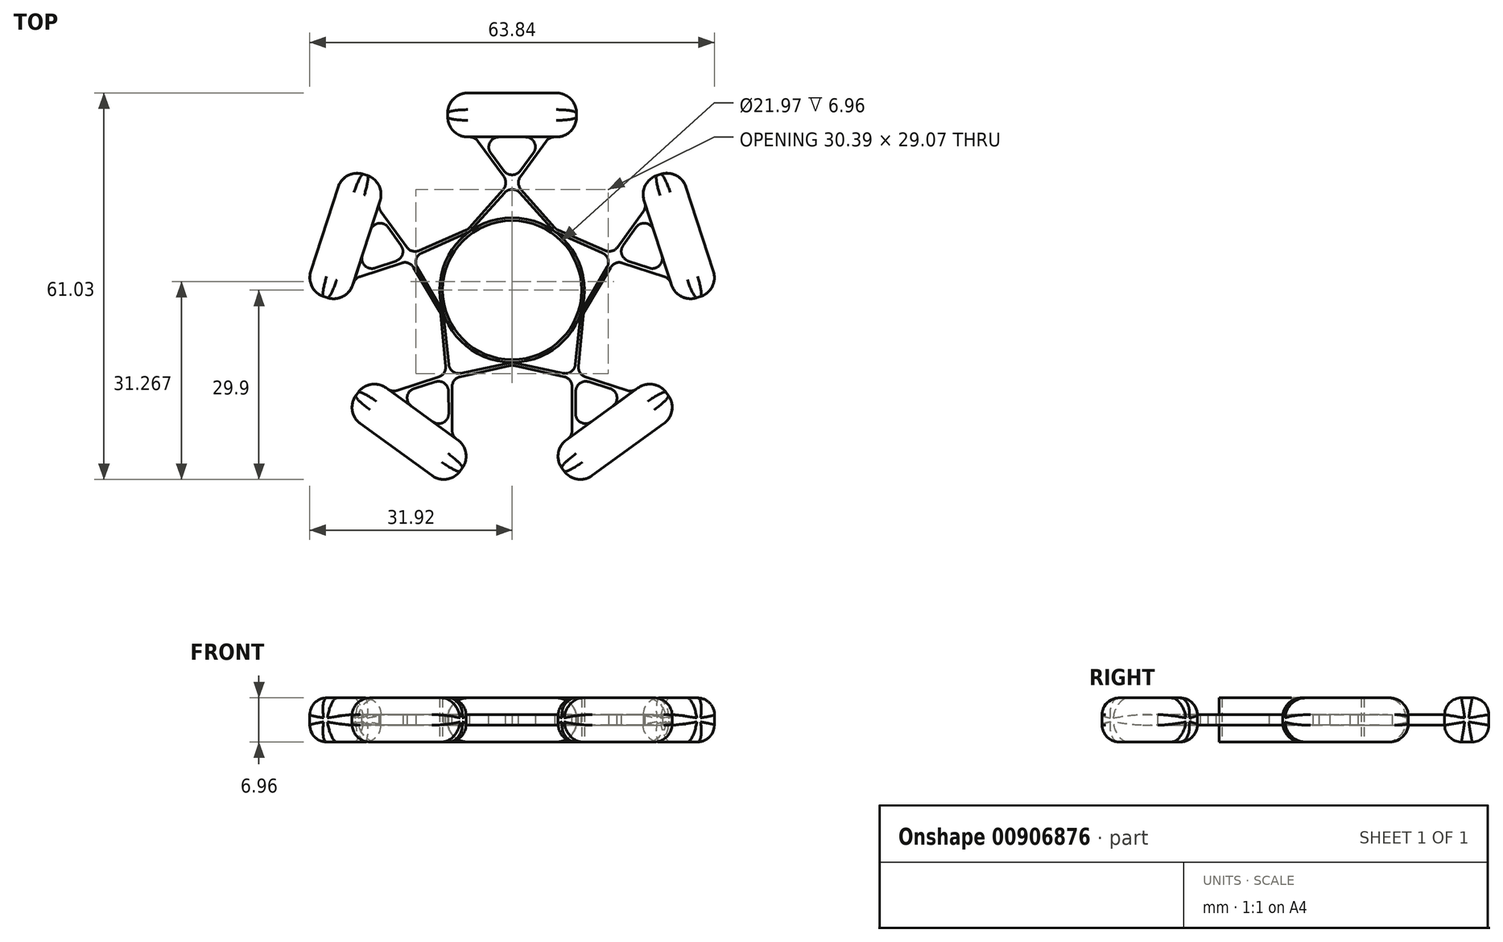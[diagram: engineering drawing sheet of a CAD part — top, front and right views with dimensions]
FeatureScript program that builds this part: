
annotation { "Feature Type Name" : "Feature", "Feature Type Description" : "" }
export const myFeature = defineFeature(function(context is Context, id is Id, definition is map)
    precondition{}
    {
        {
            var Q0;
            Q0=qCreatedBy(makeId("Top.planeOp"),FACE);
            var sketch = newSketch(context, id + "F0", { "sketchPlane" : qUnion([Q0])});
            skCircle(sketch, "E0", {"center": v(0, 0) * mm, "radius": 11.43 * mm});
            skCircle(sketch, "E1", {"center": v(0, 0) * mm, "radius": 10.99 * mm});
            skSolve(sketch);
        }
        {
            var Q0;
            Q0=makeQuery(id+"F0.imprint","IMPRINT",FACE,{"disambiguationData":[TD([[makeQuery(id+"F0.imprint","IMPRINT",EDGE,{"derivedFrom":sQuery(id+"F0.wireOp",EDGE,"E0")}),1.0]])]});
            extrude(context, id + "F1", {"entities" : qUnion([Q0]), "depth" : 6.96 * mm, "offsetDistance" : 25.4 * mm, "symmetric" : true});
        }
        {
            var Q0;
            Q0=qCreatedBy(makeId("Top.planeOp"),FACE);
            var sketch = newSketch(context, id + "F2", { "sketchPlane" : qUnion([Q0])});
            skLineSegment(sketch, "E2", {"start": v(-6.97, 9.58) * mm, "end": v(-0.55, 16.86) * mm});
            skLineSegment(sketch, "E3", {"start": v(-0.55, 16.86) * mm, "end": v(-5.87, 24.17) * mm});
            skLineSegment(sketch, "E4", {"start": v(-6.71, 9.24) * mm, "end": v(0, 16.69) * mm});
            skLineSegment(sketch, "E5", {"start": v(-5.25, 24.17) * mm, "end": v(0, 17.12) * mm});
            skLineSegment(sketch, "E6.MirrorCS", {"start": v(5.25, 24.17) * mm, "end": v(0, 17.12) * mm});
            skLineSegment(sketch, "E7.MirrorCS", {"start": v(6.71, 9.24) * mm, "end": v(0, 16.69) * mm});
            skLineSegment(sketch, "E8.MirrorCS", {"start": v(0.55, 16.86) * mm, "end": v(5.87, 24.17) * mm});
            skLineSegment(sketch, "E9.MirrorCS", {"start": v(6.97, 9.58) * mm, "end": v(0.55, 16.86) * mm});
            skLineSegment(sketch, "E10.1.0", {"start": v(-21.37, 12.47) * mm, "end": v(-16.28, 5.3) * mm});
            skLineSegment(sketch, "E10.1.1", {"start": v(-16.2, 4.68) * mm, "end": v(-24.8, 1.88) * mm});
            skLineSegment(sketch, "E10.1.2", {"start": v(-11.27, -3.67) * mm, "end": v(-16.2, 4.68) * mm});
            skLineSegment(sketch, "E10.1.3", {"start": v(-6.71, 9.24) * mm, "end": v(-15.87, 5.16) * mm});
            skLineSegment(sketch, "E10.1.4", {"start": v(-15.86, 5.74) * mm, "end": v(-21.18, 13.06) * mm});
            skLineSegment(sketch, "E10.1.5", {"start": v(-6.96, 9.6) * mm, "end": v(-15.86, 5.74) * mm});
            skLineSegment(sketch, "E10.1.6", {"start": v(-10.86, -3.53) * mm, "end": v(-15.87, 5.16) * mm});
            skLineSegment(sketch, "E10.1.7", {"start": v(-24.61, 2.47) * mm, "end": v(-16.28, 5.3) * mm});
            skLineSegment(sketch, "E10.2.0", {"start": v(-18.46, -16.47) * mm, "end": v(-10.06, -13.85) * mm});
            skLineSegment(sketch, "E10.2.1", {"start": v(-9.46, -13.97) * mm, "end": v(-9.46, -23) * mm});
            skLineSegment(sketch, "E10.2.2", {"start": v(0, -11.85) * mm, "end": v(-9.46, -13.97) * mm});
            skLineSegment(sketch, "E10.2.3", {"start": v(-10.86, -3.53) * mm, "end": v(-9.8, -13.5) * mm});
            skLineSegment(sketch, "E10.2.4", {"start": v(-10.36, -13.32) * mm, "end": v(-18.96, -16.1) * mm});
            skLineSegment(sketch, "E10.2.5", {"start": v(-11.27, -3.65) * mm, "end": v(-10.36, -13.32) * mm});
            skLineSegment(sketch, "E10.2.6", {"start": v(0, -11.42) * mm, "end": v(-9.8, -13.5) * mm});
            skLineSegment(sketch, "E10.2.7", {"start": v(-9.96, -22.65) * mm, "end": v(-10.06, -13.85) * mm});
            skLineSegment(sketch, "E10.3.0", {"start": v(9.96, -22.65) * mm, "end": v(10.06, -13.85) * mm});
            skLineSegment(sketch, "E10.3.1", {"start": v(10.36, -13.32) * mm, "end": v(18.96, -16.1) * mm});
            skLineSegment(sketch, "E10.3.2", {"start": v(11.27, -3.65) * mm, "end": v(10.36, -13.32) * mm});
            skLineSegment(sketch, "E10.3.3", {"start": v(0, -11.42) * mm, "end": v(9.8, -13.5) * mm});
            skLineSegment(sketch, "E10.3.4", {"start": v(9.46, -13.97) * mm, "end": v(9.46, -23) * mm});
            skLineSegment(sketch, "E10.3.5", {"start": v(0, -11.85) * mm, "end": v(9.46, -13.97) * mm});
            skLineSegment(sketch, "E10.3.6", {"start": v(10.86, -3.53) * mm, "end": v(9.8, -13.5) * mm});
            skLineSegment(sketch, "E10.3.7", {"start": v(18.46, -16.47) * mm, "end": v(10.06, -13.85) * mm});
            skLineSegment(sketch, "E10.4.0", {"start": v(24.61, 2.47) * mm, "end": v(16.28, 5.3) * mm});
            skLineSegment(sketch, "E10.4.1", {"start": v(15.86, 5.74) * mm, "end": v(21.18, 13.06) * mm});
            skLineSegment(sketch, "E10.4.2", {"start": v(6.96, 9.6) * mm, "end": v(15.86, 5.74) * mm});
            skLineSegment(sketch, "E10.4.3", {"start": v(10.86, -3.53) * mm, "end": v(15.87, 5.16) * mm});
            skLineSegment(sketch, "E10.4.4", {"start": v(16.2, 4.68) * mm, "end": v(24.8, 1.88) * mm});
            skLineSegment(sketch, "E10.4.5", {"start": v(11.27, -3.67) * mm, "end": v(16.2, 4.68) * mm});
            skLineSegment(sketch, "E10.4.6", {"start": v(6.71, 9.24) * mm, "end": v(15.87, 5.16) * mm});
            skLineSegment(sketch, "E10.4.7", {"start": v(21.37, 12.47) * mm, "end": v(16.28, 5.3) * mm});
            skPoint(sketch, "E10.center", {"position": v(0, 0) * mm});
            skLineSegment(sketch, "E11", {"start": v(-5.87, 24.17) * mm, "end": v(-5.25, 24.17) * mm});
            skLineSegment(sketch, "E12.MirrorCS", {"start": v(5.87, 24.17) * mm, "end": v(5.25, 24.17) * mm});
            skLineSegment(sketch, "E13.1.0", {"start": v(-21.18, 13.06) * mm, "end": v(-21.37, 12.47) * mm});
            skLineSegment(sketch, "E13.1.1", {"start": v(-24.8, 1.88) * mm, "end": v(-24.61, 2.47) * mm});
            skLineSegment(sketch, "E13.2.0", {"start": v(-18.96, -16.1) * mm, "end": v(-18.46, -16.47) * mm});
            skLineSegment(sketch, "E13.2.1", {"start": v(-9.46, -23) * mm, "end": v(-9.96, -22.65) * mm});
            skLineSegment(sketch, "E13.3.0", {"start": v(9.46, -23) * mm, "end": v(9.96, -22.65) * mm});
            skLineSegment(sketch, "E13.3.1", {"start": v(18.96, -16.1) * mm, "end": v(18.46, -16.47) * mm});
            skLineSegment(sketch, "E13.4.0", {"start": v(24.8, 1.88) * mm, "end": v(24.61, 2.47) * mm});
            skLineSegment(sketch, "E13.4.1", {"start": v(21.18, 13.06) * mm, "end": v(21.37, 12.47) * mm});
            skSolve(sketch);
        }
        {
            var Q0;
            Q0 = qSketchRegion(id + "F2", true);
            extrude(context, id + "F3", {"entities" : qUnion([Q0]), "depth" : 1.65 * mm, "offsetDistance" : 25.4 * mm, "symmetric" : true});
        }
        {
            var Q0;
            Q0=qCreatedBy(makeId("Top.planeOp"),FACE);
            var sketch = newSketch(context, id + "F4", { "sketchPlane" : qUnion([Q0])});
            skLineSegment(sketch, "E14.bottom", {"start": v(10.16, 24.17) * mm, "end": v(-10.16, 24.17) * mm});
            skLineSegment(sketch, "E14.top", {"start": v(10.16, 31.13) * mm, "end": v(-10.16, 31.13) * mm});
            skLineSegment(sketch, "E14.left", {"start": v(10.16, 24.17) * mm, "end": v(10.16, 31.13) * mm});
            skLineSegment(sketch, "E14.right", {"start": v(-10.16, 24.17) * mm, "end": v(-10.16, 31.13) * mm});
            skPoint(sketch, "E14.middle", {"position": v(0, 27.65) * mm});
            skLineSegment(sketch, "E15.1.0", {"start": v(-19.85, 17.13) * mm, "end": v(-26.13, -2.2) * mm});
            skPoint(sketch, "E15.1.1", {"position": v(-26.3, 8.55) * mm});
            skLineSegment(sketch, "E15.1.2", {"start": v(-19.85, 17.13) * mm, "end": v(-26.47, 19.28) * mm});
            skLineSegment(sketch, "E15.1.3", {"start": v(-26.47, 19.28) * mm, "end": v(-32.75, -0.04) * mm});
            skLineSegment(sketch, "E15.1.4", {"start": v(-26.13, -2.2) * mm, "end": v(-32.75, -0.04) * mm});
            skLineSegment(sketch, "E15.2.0", {"start": v(-22.43, -13.58) * mm, "end": v(-5.99, -25.53) * mm});
            skPoint(sketch, "E15.2.1", {"position": v(-16.25, -22.37) * mm});
            skLineSegment(sketch, "E15.2.2", {"start": v(-22.43, -13.58) * mm, "end": v(-26.52, -19.22) * mm});
            skLineSegment(sketch, "E15.2.3", {"start": v(-26.52, -19.22) * mm, "end": v(-10.08, -31.16) * mm});
            skLineSegment(sketch, "E15.2.4", {"start": v(-5.99, -25.53) * mm, "end": v(-10.08, -31.16) * mm});
            skLineSegment(sketch, "E15.3.0", {"start": v(5.99, -25.53) * mm, "end": v(22.43, -13.58) * mm});
            skPoint(sketch, "E15.3.1", {"position": v(16.25, -22.37) * mm});
            skLineSegment(sketch, "E15.3.2", {"start": v(5.99, -25.53) * mm, "end": v(10.08, -31.16) * mm});
            skLineSegment(sketch, "E15.3.3", {"start": v(10.08, -31.16) * mm, "end": v(26.52, -19.22) * mm});
            skLineSegment(sketch, "E15.3.4", {"start": v(22.43, -13.58) * mm, "end": v(26.52, -19.22) * mm});
            skLineSegment(sketch, "E15.4.0", {"start": v(26.13, -2.2) * mm, "end": v(19.85, 17.13) * mm});
            skPoint(sketch, "E15.4.1", {"position": v(26.3, 8.55) * mm});
            skLineSegment(sketch, "E15.4.2", {"start": v(26.13, -2.2) * mm, "end": v(32.75, -0.04) * mm});
            skLineSegment(sketch, "E15.4.3", {"start": v(32.75, -0.04) * mm, "end": v(26.47, 19.28) * mm});
            skLineSegment(sketch, "E15.4.4", {"start": v(19.85, 17.13) * mm, "end": v(26.47, 19.28) * mm});
            skPoint(sketch, "E15.center", {"position": v(0, 0) * mm});
            skSolve(sketch);
        }
        {
            var Q0;
            Q0 = qSketchRegion(id + "F4", true);
            extrude(context, id + "F5", {"entities" : qUnion([Q0]), "operationType" : NewBodyOperationType.ADD, "depth" : 6.96 * mm, "offsetDistance" : 25.4 * mm, "symmetric" : true});
        }
        {
            var Q0;
            Q0=makeQuery(id+"F3.opExtrude","SWEPT_EDGE",EDGE,{"disambiguationData":[OSD([sQuery(id+"F2.wireOp",EDGE,"E10.1.1"),sQuery(id+"F2.wireOp",EDGE,"E10.1.2")])]});
            var Q1;
            Q1=makeQuery(id+"F3.opExtrude","SWEPT_EDGE",EDGE,{"disambiguationData":[OSD([sQuery(id+"F2.wireOp",EDGE,"E10.1.4"),sQuery(id+"F2.wireOp",EDGE,"E10.1.5")])]});
            var Q2;
            Q2=makeQuery(id+"F3.opExtrude","SWEPT_EDGE",EDGE,{"disambiguationData":[OSD([sQuery(id+"F2.wireOp",EDGE,"E10.1.3"),sQuery(id+"F2.wireOp",EDGE,"E10.1.6")])]});
            var Q3;
            Q3=makeQuery(id+"F3.opExtrude","SWEPT_EDGE",EDGE,{"disambiguationData":[OSD([sQuery(id+"F2.wireOp",EDGE,"E10.1.0"),sQuery(id+"F2.wireOp",EDGE,"E10.1.7")])]});
            var Q4;
            Q4=makeQuery(id+"F5.boolean.opBoolean","INTERSECT",EDGE,{"derivedFrom":[makeQuery(id+"F3.opExtrude","SWEPT_FACE",FACE,{"disambiguationData":[OSD([sQuery(id+"F2.wireOp",EDGE,"E10.1.0")])]}),makeQuery(id+"F5.opExtrude","SWEPT_FACE",FACE,{"disambiguationData":[OSD([sQuery(id+"F4.wireOp",EDGE,"E15.1.0")])]})]});
            var Q5;
            Q5=makeQuery(id+"F5.boolean.opBoolean","INTERSECT",EDGE,{"derivedFrom":[makeQuery(id+"F3.opExtrude","SWEPT_FACE",FACE,{"disambiguationData":[OSD([sQuery(id+"F2.wireOp",EDGE,"E10.1.1")])]}),makeQuery(id+"F5.opExtrude","SWEPT_FACE",FACE,{"disambiguationData":[OSD([sQuery(id+"F4.wireOp",EDGE,"E15.1.0")])]})]});
            var Q6;
            Q6=makeQuery(id+"F5.boolean.opBoolean","INTERSECT",EDGE,{"derivedFrom":[makeQuery(id+"F3.opExtrude","SWEPT_FACE",FACE,{"disambiguationData":[OSD([sQuery(id+"F2.wireOp",EDGE,"E10.1.7")])]}),makeQuery(id+"F5.opExtrude","SWEPT_FACE",FACE,{"disambiguationData":[OSD([sQuery(id+"F4.wireOp",EDGE,"E15.1.0")])]})]});
            var Q7;
            Q7=makeQuery(id+"F5.boolean.opBoolean","INTERSECT",EDGE,{"derivedFrom":[makeQuery(id+"F3.opExtrude","SWEPT_FACE",FACE,{"disambiguationData":[OSD([sQuery(id+"F2.wireOp",EDGE,"E10.1.4")])]}),makeQuery(id+"F5.opExtrude","SWEPT_FACE",FACE,{"disambiguationData":[OSD([sQuery(id+"F4.wireOp",EDGE,"E15.1.0")])]})]});
            var Q8;
            Q8=makeQuery(id+"F3.opExtrude","SWEPT_EDGE",EDGE,{"disambiguationData":[OSD([sQuery(id+"F2.wireOp",EDGE,"E2"),sQuery(id+"F2.wireOp",EDGE,"E10.1.5")])]});
            var Q9;
            Q9=makeQuery(id+"F3.opExtrude","SWEPT_EDGE",EDGE,{"disambiguationData":[OSD([sQuery(id+"F2.wireOp",EDGE,"E10.1.2"),sQuery(id+"F2.wireOp",EDGE,"E10.2.5")])]});
            var Q10;
            Q10=makeQuery(id+"F3.opExtrude","SWEPT_EDGE",EDGE,{"disambiguationData":[OSD([sQuery(id+"F2.wireOp",EDGE,"E8.MirrorCS"),sQuery(id+"F2.wireOp",EDGE,"E9.MirrorCS")])]});
            var Q11;
            Q11=makeQuery(id+"F3.opExtrude","SWEPT_EDGE",EDGE,{"disambiguationData":[OSD([sQuery(id+"F2.wireOp",EDGE,"E9.MirrorCS"),sQuery(id+"F2.wireOp",EDGE,"E10.4.2")])]});
            var Q12;
            Q12=makeQuery(id+"F3.opExtrude","SWEPT_EDGE",EDGE,{"disambiguationData":[OSD([sQuery(id+"F2.wireOp",EDGE,"E2"),sQuery(id+"F2.wireOp",EDGE,"E3")])]});
            var Q13;
            Q13=makeQuery(id+"F3.opExtrude","SWEPT_EDGE",EDGE,{"disambiguationData":[OSD([sQuery(id+"F2.wireOp",EDGE,"E4"),sQuery(id+"F2.wireOp",EDGE,"E7.MirrorCS")])]});
            var Q14;
            Q14=makeQuery(id+"F3.opExtrude","SWEPT_EDGE",EDGE,{"disambiguationData":[OSD([sQuery(id+"F2.wireOp",EDGE,"E5"),sQuery(id+"F2.wireOp",EDGE,"E6.MirrorCS")])]});
            var Q15;
            Q15=makeQuery(id+"F5.boolean.opBoolean","INTERSECT",EDGE,{"derivedFrom":[makeQuery(id+"F3.opExtrude","SWEPT_FACE",FACE,{"disambiguationData":[OSD([sQuery(id+"F2.wireOp",EDGE,"E8.MirrorCS")])]}),makeQuery(id+"F5.opExtrude","SWEPT_FACE",FACE,{"disambiguationData":[OSD([sQuery(id+"F4.wireOp",EDGE,"E14.bottom")])]})]});
            var Q16;
            Q16=makeQuery(id+"F5.boolean.opBoolean","INTERSECT",EDGE,{"derivedFrom":[makeQuery(id+"F3.opExtrude","SWEPT_FACE",FACE,{"disambiguationData":[OSD([sQuery(id+"F2.wireOp",EDGE,"E3")])]}),makeQuery(id+"F5.opExtrude","SWEPT_FACE",FACE,{"disambiguationData":[OSD([sQuery(id+"F4.wireOp",EDGE,"E14.bottom")])]})]});
            var Q17;
            Q17=makeQuery(id+"F5.boolean.opBoolean","INTERSECT",EDGE,{"derivedFrom":[makeQuery(id+"F3.opExtrude","SWEPT_FACE",FACE,{"disambiguationData":[OSD([sQuery(id+"F2.wireOp",EDGE,"E5")])]}),makeQuery(id+"F5.opExtrude","SWEPT_FACE",FACE,{"disambiguationData":[OSD([sQuery(id+"F4.wireOp",EDGE,"E14.bottom")])]})]});
            var Q18;
            Q18=makeQuery(id+"F5.boolean.opBoolean","INTERSECT",EDGE,{"derivedFrom":[makeQuery(id+"F3.opExtrude","SWEPT_FACE",FACE,{"disambiguationData":[OSD([sQuery(id+"F2.wireOp",EDGE,"E6.MirrorCS")])]}),makeQuery(id+"F5.opExtrude","SWEPT_FACE",FACE,{"disambiguationData":[OSD([sQuery(id+"F4.wireOp",EDGE,"E14.bottom")])]})]});
            var Q19;
            Q19=makeQuery(id+"F3.opExtrude","SWEPT_EDGE",EDGE,{"disambiguationData":[OSD([sQuery(id+"F2.wireOp",EDGE,"E10.4.4"),sQuery(id+"F2.wireOp",EDGE,"E10.4.5")])]});
            var Q20;
            Q20=makeQuery(id+"F3.opExtrude","SWEPT_EDGE",EDGE,{"disambiguationData":[OSD([sQuery(id+"F2.wireOp",EDGE,"E10.3.2"),sQuery(id+"F2.wireOp",EDGE,"E10.4.5")])]});
            var Q21;
            Q21=makeQuery(id+"F5.boolean.opBoolean","INTERSECT",EDGE,{"derivedFrom":[makeQuery(id+"F3.opExtrude","SWEPT_FACE",FACE,{"disambiguationData":[OSD([sQuery(id+"F2.wireOp",EDGE,"E10.4.1")])]}),makeQuery(id+"F5.opExtrude","SWEPT_FACE",FACE,{"disambiguationData":[OSD([sQuery(id+"F4.wireOp",EDGE,"E15.4.0")])]})]});
            var Q22;
            Q22=makeQuery(id+"F3.opExtrude","SWEPT_EDGE",EDGE,{"disambiguationData":[OSD([sQuery(id+"F2.wireOp",EDGE,"E10.4.3"),sQuery(id+"F2.wireOp",EDGE,"E10.4.6")])]});
            var Q23;
            Q23=makeQuery(id+"F5.boolean.opBoolean","INTERSECT",EDGE,{"derivedFrom":[makeQuery(id+"F3.opExtrude","SWEPT_FACE",FACE,{"disambiguationData":[OSD([sQuery(id+"F2.wireOp",EDGE,"E10.4.4")])]}),makeQuery(id+"F5.opExtrude","SWEPT_FACE",FACE,{"disambiguationData":[OSD([sQuery(id+"F4.wireOp",EDGE,"E15.4.0")])]})]});
            var Q24;
            Q24=makeQuery(id+"F3.opExtrude","SWEPT_EDGE",EDGE,{"disambiguationData":[OSD([sQuery(id+"F2.wireOp",EDGE,"E10.4.0"),sQuery(id+"F2.wireOp",EDGE,"E10.4.7")])]});
            var Q25;
            Q25=makeQuery(id+"F3.opExtrude","SWEPT_EDGE",EDGE,{"disambiguationData":[OSD([sQuery(id+"F2.wireOp",EDGE,"E10.4.1"),sQuery(id+"F2.wireOp",EDGE,"E10.4.2")])]});
            var Q26;
            Q26=makeQuery(id+"F5.boolean.opBoolean","INTERSECT",EDGE,{"derivedFrom":[makeQuery(id+"F3.opExtrude","SWEPT_FACE",FACE,{"disambiguationData":[OSD([sQuery(id+"F2.wireOp",EDGE,"E10.4.7")])]}),makeQuery(id+"F5.opExtrude","SWEPT_FACE",FACE,{"disambiguationData":[OSD([sQuery(id+"F4.wireOp",EDGE,"E15.4.0")])]})]});
            var Q27;
            Q27=makeQuery(id+"F5.boolean.opBoolean","INTERSECT",EDGE,{"derivedFrom":[makeQuery(id+"F3.opExtrude","SWEPT_FACE",FACE,{"disambiguationData":[OSD([sQuery(id+"F2.wireOp",EDGE,"E10.4.0")])]}),makeQuery(id+"F5.opExtrude","SWEPT_FACE",FACE,{"disambiguationData":[OSD([sQuery(id+"F4.wireOp",EDGE,"E15.4.0")])]})]});
            var Q28;
            Q28=makeQuery(id+"F3.opExtrude","SWEPT_EDGE",EDGE,{"disambiguationData":[OSD([sQuery(id+"F2.wireOp",EDGE,"E10.2.2"),sQuery(id+"F2.wireOp",EDGE,"E10.3.5")])]});
            var Q29;
            Q29=makeQuery(id+"F3.opExtrude","SWEPT_EDGE",EDGE,{"disambiguationData":[OSD([sQuery(id+"F2.wireOp",EDGE,"E10.3.1"),sQuery(id+"F2.wireOp",EDGE,"E10.3.2")])]});
            var Q30;
            Q30=makeQuery(id+"F3.opExtrude","SWEPT_EDGE",EDGE,{"disambiguationData":[OSD([sQuery(id+"F2.wireOp",EDGE,"E10.3.4"),sQuery(id+"F2.wireOp",EDGE,"E10.3.5")])]});
            var Q31;
            Q31=makeQuery(id+"F3.opExtrude","SWEPT_EDGE",EDGE,{"disambiguationData":[OSD([sQuery(id+"F2.wireOp",EDGE,"E10.3.3"),sQuery(id+"F2.wireOp",EDGE,"E10.3.6")])]});
            var Q32;
            Q32=makeQuery(id+"F3.opExtrude","SWEPT_EDGE",EDGE,{"disambiguationData":[OSD([sQuery(id+"F2.wireOp",EDGE,"E10.3.0"),sQuery(id+"F2.wireOp",EDGE,"E10.3.7")])]});
            var Q33;
            Q33=makeQuery(id+"F5.boolean.opBoolean","INTERSECT",EDGE,{"derivedFrom":[makeQuery(id+"F3.opExtrude","SWEPT_FACE",FACE,{"disambiguationData":[OSD([sQuery(id+"F2.wireOp",EDGE,"E10.3.4")])]}),makeQuery(id+"F5.opExtrude","SWEPT_FACE",FACE,{"disambiguationData":[OSD([sQuery(id+"F4.wireOp",EDGE,"E15.3.0")])]})]});
            var Q34;
            Q34=makeQuery(id+"F5.boolean.opBoolean","INTERSECT",EDGE,{"derivedFrom":[makeQuery(id+"F3.opExtrude","SWEPT_FACE",FACE,{"disambiguationData":[OSD([sQuery(id+"F2.wireOp",EDGE,"E10.3.1")])]}),makeQuery(id+"F5.opExtrude","SWEPT_FACE",FACE,{"disambiguationData":[OSD([sQuery(id+"F4.wireOp",EDGE,"E15.3.0")])]})]});
            var Q35;
            Q35=makeQuery(id+"F5.boolean.opBoolean","INTERSECT",EDGE,{"derivedFrom":[makeQuery(id+"F3.opExtrude","SWEPT_FACE",FACE,{"disambiguationData":[OSD([sQuery(id+"F2.wireOp",EDGE,"E10.3.7")])]}),makeQuery(id+"F5.opExtrude","SWEPT_FACE",FACE,{"disambiguationData":[OSD([sQuery(id+"F4.wireOp",EDGE,"E15.3.0")])]})]});
            var Q36;
            Q36=makeQuery(id+"F5.boolean.opBoolean","INTERSECT",EDGE,{"derivedFrom":[makeQuery(id+"F3.opExtrude","SWEPT_FACE",FACE,{"disambiguationData":[OSD([sQuery(id+"F2.wireOp",EDGE,"E10.3.0")])]}),makeQuery(id+"F5.opExtrude","SWEPT_FACE",FACE,{"disambiguationData":[OSD([sQuery(id+"F4.wireOp",EDGE,"E15.3.0")])]})]});
            var Q37;
            Q37=makeQuery(id+"F5.boolean.opBoolean","INTERSECT",EDGE,{"derivedFrom":[makeQuery(id+"F3.opExtrude","SWEPT_FACE",FACE,{"disambiguationData":[OSD([sQuery(id+"F2.wireOp",EDGE,"E10.2.4")])]}),makeQuery(id+"F5.opExtrude","SWEPT_FACE",FACE,{"disambiguationData":[OSD([sQuery(id+"F4.wireOp",EDGE,"E15.2.0")])]})]});
            var Q38;
            Q38=makeQuery(id+"F3.opExtrude","SWEPT_EDGE",EDGE,{"disambiguationData":[OSD([sQuery(id+"F2.wireOp",EDGE,"E10.2.4"),sQuery(id+"F2.wireOp",EDGE,"E10.2.5")])]});
            var Q39;
            Q39=makeQuery(id+"F5.boolean.opBoolean","INTERSECT",EDGE,{"derivedFrom":[makeQuery(id+"F3.opExtrude","SWEPT_FACE",FACE,{"disambiguationData":[OSD([sQuery(id+"F2.wireOp",EDGE,"E10.2.7")])]}),makeQuery(id+"F5.opExtrude","SWEPT_FACE",FACE,{"disambiguationData":[OSD([sQuery(id+"F4.wireOp",EDGE,"E15.2.0")])]})]});
            var Q40;
            Q40=makeQuery(id+"F5.boolean.opBoolean","INTERSECT",EDGE,{"derivedFrom":[makeQuery(id+"F3.opExtrude","SWEPT_FACE",FACE,{"disambiguationData":[OSD([sQuery(id+"F2.wireOp",EDGE,"E10.2.0")])]}),makeQuery(id+"F5.opExtrude","SWEPT_FACE",FACE,{"disambiguationData":[OSD([sQuery(id+"F4.wireOp",EDGE,"E15.2.0")])]})]});
            var Q41;
            Q41=makeQuery(id+"F5.boolean.opBoolean","INTERSECT",EDGE,{"derivedFrom":[makeQuery(id+"F3.opExtrude","SWEPT_FACE",FACE,{"disambiguationData":[OSD([sQuery(id+"F2.wireOp",EDGE,"E10.2.1")])]}),makeQuery(id+"F5.opExtrude","SWEPT_FACE",FACE,{"disambiguationData":[OSD([sQuery(id+"F4.wireOp",EDGE,"E15.2.0")])]})]});
            var Q42;
            Q42=makeQuery(id+"F3.opExtrude","SWEPT_EDGE",EDGE,{"disambiguationData":[OSD([sQuery(id+"F2.wireOp",EDGE,"E10.2.1"),sQuery(id+"F2.wireOp",EDGE,"E10.2.2")])]});
            var Q43;
            Q43=makeQuery(id+"F3.opExtrude","SWEPT_EDGE",EDGE,{"disambiguationData":[OSD([sQuery(id+"F2.wireOp",EDGE,"E3"),sQuery(id+"F2.wireOp",EDGE,"E11")])]});
            var Q44;
            Q44=makeQuery(id+"F3.opExtrude","SWEPT_EDGE",EDGE,{"disambiguationData":[OSD([sQuery(id+"F2.wireOp",EDGE,"E6.MirrorCS"),sQuery(id+"F2.wireOp",EDGE,"E12.MirrorCS")])]});
            var Q45;
            Q45=makeQuery(id+"F3.opExtrude","SWEPT_EDGE",EDGE,{"disambiguationData":[OSD([sQuery(id+"F2.wireOp",EDGE,"E5"),sQuery(id+"F2.wireOp",EDGE,"E11")])]});
            var Q46;
            Q46=makeQuery(id+"F3.opExtrude","SWEPT_EDGE",EDGE,{"disambiguationData":[OSD([sQuery(id+"F2.wireOp",EDGE,"E8.MirrorCS"),sQuery(id+"F2.wireOp",EDGE,"E12.MirrorCS")])]});
            var Q47;
            Q47=makeQuery(id+"F3.opExtrude","SWEPT_EDGE",EDGE,{"disambiguationData":[OSD([sQuery(id+"F2.wireOp",EDGE,"E10.4.1"),sQuery(id+"F2.wireOp",EDGE,"E13.4.1")])]});
            var Q48;
            Q48=makeQuery(id+"F3.opExtrude","SWEPT_EDGE",EDGE,{"disambiguationData":[OSD([sQuery(id+"F2.wireOp",EDGE,"E10.4.4"),sQuery(id+"F2.wireOp",EDGE,"E13.4.0")])]});
            var Q49;
            Q49=makeQuery(id+"F3.opExtrude","SWEPT_EDGE",EDGE,{"disambiguationData":[OSD([sQuery(id+"F2.wireOp",EDGE,"E10.4.7"),sQuery(id+"F2.wireOp",EDGE,"E13.4.1")])]});
            var Q50;
            Q50=makeQuery(id+"F3.opExtrude","SWEPT_EDGE",EDGE,{"disambiguationData":[OSD([sQuery(id+"F2.wireOp",EDGE,"E10.4.0"),sQuery(id+"F2.wireOp",EDGE,"E13.4.0")])]});
            var Q51;
            Q51=makeQuery(id+"F3.opExtrude","SWEPT_EDGE",EDGE,{"disambiguationData":[OSD([sQuery(id+"F2.wireOp",EDGE,"E10.3.4"),sQuery(id+"F2.wireOp",EDGE,"E13.3.0")])]});
            var Q52;
            Q52=makeQuery(id+"F3.opExtrude","SWEPT_EDGE",EDGE,{"disambiguationData":[OSD([sQuery(id+"F2.wireOp",EDGE,"E10.3.0"),sQuery(id+"F2.wireOp",EDGE,"E13.3.0")])]});
            var Q53;
            Q53=makeQuery(id+"F3.opExtrude","SWEPT_EDGE",EDGE,{"disambiguationData":[OSD([sQuery(id+"F2.wireOp",EDGE,"E10.3.1"),sQuery(id+"F2.wireOp",EDGE,"E13.3.1")])]});
            var Q54;
            Q54=makeQuery(id+"F3.opExtrude","SWEPT_EDGE",EDGE,{"disambiguationData":[OSD([sQuery(id+"F2.wireOp",EDGE,"E10.2.1"),sQuery(id+"F2.wireOp",EDGE,"E13.2.1")])]});
            var Q55;
            Q55=makeQuery(id+"F3.opExtrude","SWEPT_EDGE",EDGE,{"disambiguationData":[OSD([sQuery(id+"F2.wireOp",EDGE,"E10.2.3"),sQuery(id+"F2.wireOp",EDGE,"E10.2.6")])]});
            var Q56;
            Q56=makeQuery(id+"F3.opExtrude","SWEPT_EDGE",EDGE,{"disambiguationData":[OSD([sQuery(id+"F2.wireOp",EDGE,"E10.3.7"),sQuery(id+"F2.wireOp",EDGE,"E13.3.1")])]});
            var Q57;
            Q57=makeQuery(id+"F3.opExtrude","SWEPT_EDGE",EDGE,{"disambiguationData":[OSD([sQuery(id+"F2.wireOp",EDGE,"E10.2.4"),sQuery(id+"F2.wireOp",EDGE,"E13.2.0")])]});
            var Q58;
            Q58=makeQuery(id+"F3.opExtrude","SWEPT_EDGE",EDGE,{"disambiguationData":[OSD([sQuery(id+"F2.wireOp",EDGE,"E10.2.7"),sQuery(id+"F2.wireOp",EDGE,"E13.2.1")])]});
            var Q59;
            Q59=makeQuery(id+"F3.opExtrude","SWEPT_EDGE",EDGE,{"disambiguationData":[OSD([sQuery(id+"F2.wireOp",EDGE,"E10.2.0"),sQuery(id+"F2.wireOp",EDGE,"E13.2.0")])]});
            var Q60;
            Q60=makeQuery(id+"F3.opExtrude","SWEPT_EDGE",EDGE,{"disambiguationData":[OSD([sQuery(id+"F2.wireOp",EDGE,"E10.1.1"),sQuery(id+"F2.wireOp",EDGE,"E13.1.1")])]});
            var Q61;
            Q61=makeQuery(id+"F3.opExtrude","SWEPT_EDGE",EDGE,{"disambiguationData":[OSD([sQuery(id+"F2.wireOp",EDGE,"E10.1.4"),sQuery(id+"F2.wireOp",EDGE,"E13.1.0")])]});
            var Q62;
            Q62=makeQuery(id+"F3.opExtrude","SWEPT_EDGE",EDGE,{"disambiguationData":[OSD([sQuery(id+"F2.wireOp",EDGE,"E10.1.7"),sQuery(id+"F2.wireOp",EDGE,"E13.1.1")])]});
            var Q63;
            Q63=makeQuery(id+"F3.opExtrude","SWEPT_EDGE",EDGE,{"disambiguationData":[OSD([sQuery(id+"F2.wireOp",EDGE,"E10.1.0"),sQuery(id+"F2.wireOp",EDGE,"E13.1.0")])]});
            var Q64;
            Q64=makeQuery(id+"F3.opExtrude","SWEPT_EDGE",EDGE,{"disambiguationData":[OSD([sQuery(id+"F2.wireOp",EDGE,"E10.2.0"),sQuery(id+"F2.wireOp",EDGE,"E10.2.7")])]});
            fillet(context, id + "F6", {"entities" : qUnion([Q0, Q1, Q2, Q3, Q4, Q5, Q6, Q7, Q8, Q9, Q10, Q11, Q12, Q13, Q14, Q15, Q16, Q17, Q18, Q19, Q20, Q21, Q22, Q23, Q24, Q25, Q26, Q27, Q28, Q29, Q30, Q31, Q32, Q33, Q34, Q35, Q36, Q37, Q38, Q39, Q40, Q41, Q42, Q43, Q44, Q45, Q46, Q47, Q48, Q49, Q50, Q51, Q52, Q53, Q54, Q55, Q56, Q57, Q58, Q59, Q60, Q61, Q62, Q63, Q64]), "radius" : 1.59 * mm, "tangentPropagation" : true, "allowEdgeOverflow" : false});
        }
        {
            var Q0;
            Q0=makeQuery(id+"F5.opExtrude","CAP_EDGE",EDGE,{"disambiguationData":[OSD([sQuery(id+"F4.wireOp",EDGE,"E14.top")])],"isStart":false});
            var Q1;
            Q1=makeQuery(id+"F5.opExtrude","CAP_EDGE",EDGE,{"disambiguationData":[OSD([sQuery(id+"F4.wireOp",EDGE,"E14.bottom")])],"isStart":false});
            var Q2;
            Q2=makeQuery(id+"F5.opExtrude","CAP_EDGE",EDGE,{"disambiguationData":[OSD([sQuery(id+"F4.wireOp",EDGE,"E14.top")])],"isStart":true});
            var Q3;
            Q3=makeQuery(id+"F5.opExtrude","CAP_EDGE",EDGE,{"disambiguationData":[OSD([sQuery(id+"F4.wireOp",EDGE,"E14.bottom")])],"isStart":true});
            var Q4;
            Q4=makeQuery(id+"F5.opExtrude","CAP_EDGE",EDGE,{"disambiguationData":[OSD([sQuery(id+"F4.wireOp",EDGE,"E15.4.3")])],"isStart":false});
            var Q5;
            Q5=makeQuery(id+"F5.opExtrude","CAP_EDGE",EDGE,{"disambiguationData":[OSD([sQuery(id+"F4.wireOp",EDGE,"E15.4.3")])],"isStart":true});
            var Q6;
            Q6=makeQuery(id+"F5.opExtrude","CAP_EDGE",EDGE,{"disambiguationData":[OSD([sQuery(id+"F4.wireOp",EDGE,"E15.4.0")])],"isStart":true});
            var Q7;
            Q7=makeQuery(id+"F5.opExtrude","CAP_EDGE",EDGE,{"disambiguationData":[OSD([sQuery(id+"F4.wireOp",EDGE,"E15.4.0")])],"isStart":false});
            var Q8;
            Q8=makeQuery(id+"F5.opExtrude","CAP_EDGE",EDGE,{"disambiguationData":[OSD([sQuery(id+"F4.wireOp",EDGE,"E15.3.3")])],"isStart":false});
            var Q9;
            Q9=makeQuery(id+"F5.opExtrude","CAP_EDGE",EDGE,{"disambiguationData":[OSD([sQuery(id+"F4.wireOp",EDGE,"E15.3.3")])],"isStart":true});
            var Q10;
            Q10=makeQuery(id+"F5.opExtrude","CAP_EDGE",EDGE,{"disambiguationData":[OSD([sQuery(id+"F4.wireOp",EDGE,"E15.3.0")])],"isStart":true});
            var Q11;
            Q11=makeQuery(id+"F5.opExtrude","CAP_EDGE",EDGE,{"disambiguationData":[OSD([sQuery(id+"F4.wireOp",EDGE,"E15.3.0")])],"isStart":false});
            var Q12;
            Q12=makeQuery(id+"F5.opExtrude","CAP_EDGE",EDGE,{"disambiguationData":[OSD([sQuery(id+"F4.wireOp",EDGE,"E15.2.3")])],"isStart":false});
            var Q13;
            Q13=makeQuery(id+"F5.opExtrude","CAP_EDGE",EDGE,{"disambiguationData":[OSD([sQuery(id+"F4.wireOp",EDGE,"E15.2.3")])],"isStart":true});
            var Q14;
            Q14=makeQuery(id+"F5.opExtrude","CAP_EDGE",EDGE,{"disambiguationData":[OSD([sQuery(id+"F4.wireOp",EDGE,"E15.2.0")])],"isStart":false});
            var Q15;
            Q15=makeQuery(id+"F5.opExtrude","CAP_EDGE",EDGE,{"disambiguationData":[OSD([sQuery(id+"F4.wireOp",EDGE,"E15.2.0")])],"isStart":true});
            var Q16;
            Q16=makeQuery(id+"F5.opExtrude","CAP_EDGE",EDGE,{"disambiguationData":[OSD([sQuery(id+"F4.wireOp",EDGE,"E15.1.3")])],"isStart":true});
            var Q17;
            Q17=makeQuery(id+"F5.opExtrude","CAP_EDGE",EDGE,{"disambiguationData":[OSD([sQuery(id+"F4.wireOp",EDGE,"E15.1.3")])],"isStart":false});
            var Q18;
            Q18=makeQuery(id+"F5.opExtrude","CAP_EDGE",EDGE,{"disambiguationData":[OSD([sQuery(id+"F4.wireOp",EDGE,"E15.1.0")])],"isStart":false});
            var Q19;
            Q19=makeQuery(id+"F5.opExtrude","CAP_EDGE",EDGE,{"disambiguationData":[OSD([sQuery(id+"F4.wireOp",EDGE,"E15.1.0")])],"isStart":true});
            fillet(context, id + "F7", {"entities" : qUnion([Q0, Q1, Q2, Q3, Q4, Q5, Q6, Q7, Q8, Q9, Q10, Q11, Q12, Q13, Q14, Q15, Q16, Q17, Q18, Q19]), "radius" : 2.64 * mm, "tangentPropagation" : true, "allowEdgeOverflow" : false});
        }
        {
            var Q0;
            Q0=makeQuery(id+"F5.opExtrude","SWEPT_FACE",FACE,{"disambiguationData":[OSD([sQuery(id+"F4.wireOp",EDGE,"E14.left")])]});
            var Q1;
            Q1=makeQuery(id+"F5.opExtrude","SWEPT_FACE",FACE,{"disambiguationData":[OSD([sQuery(id+"F4.wireOp",EDGE,"E14.right")])]});
            var Q2;
            Q2=makeQuery(id+"F5.opExtrude","SWEPT_FACE",FACE,{"disambiguationData":[OSD([sQuery(id+"F4.wireOp",EDGE,"E15.4.2")])]});
            var Q3;
            Q3=makeQuery(id+"F5.opExtrude","SWEPT_FACE",FACE,{"disambiguationData":[OSD([sQuery(id+"F4.wireOp",EDGE,"E15.2.4")])]});
            var Q4;
            Q4=makeQuery(id+"F5.opExtrude","SWEPT_FACE",FACE,{"disambiguationData":[OSD([sQuery(id+"F4.wireOp",EDGE,"E15.1.4")])]});
            var Q5;
            Q5=makeQuery(id+"F5.opExtrude","SWEPT_FACE",FACE,{"disambiguationData":[OSD([sQuery(id+"F4.wireOp",EDGE,"E15.3.2")])]});
            var Q6;
            Q6=makeQuery(id+"F5.opExtrude","SWEPT_FACE",FACE,{"disambiguationData":[OSD([sQuery(id+"F4.wireOp",EDGE,"E15.2.2")])]});
            var Q7;
            Q7=makeQuery(id+"F5.opExtrude","SWEPT_FACE",FACE,{"disambiguationData":[OSD([sQuery(id+"F4.wireOp",EDGE,"E15.4.4")])]});
            var Q8;
            Q8=makeQuery(id+"F5.opExtrude","SWEPT_FACE",FACE,{"disambiguationData":[OSD([sQuery(id+"F4.wireOp",EDGE,"E15.1.2")])]});
            var Q9;
            Q9=makeQuery(id+"F5.opExtrude","SWEPT_FACE",FACE,{"disambiguationData":[OSD([sQuery(id+"F4.wireOp",EDGE,"E15.3.4")])]});
            fillet(context, id + "F8", {"entities" : qUnion([Q0, Q1, Q2, Q3, Q4, Q5, Q6, Q7, Q8, Q9]), "radius" : 3.17 * mm, "tangentPropagation" : true, "allowEdgeOverflow" : false});
        }
    });
